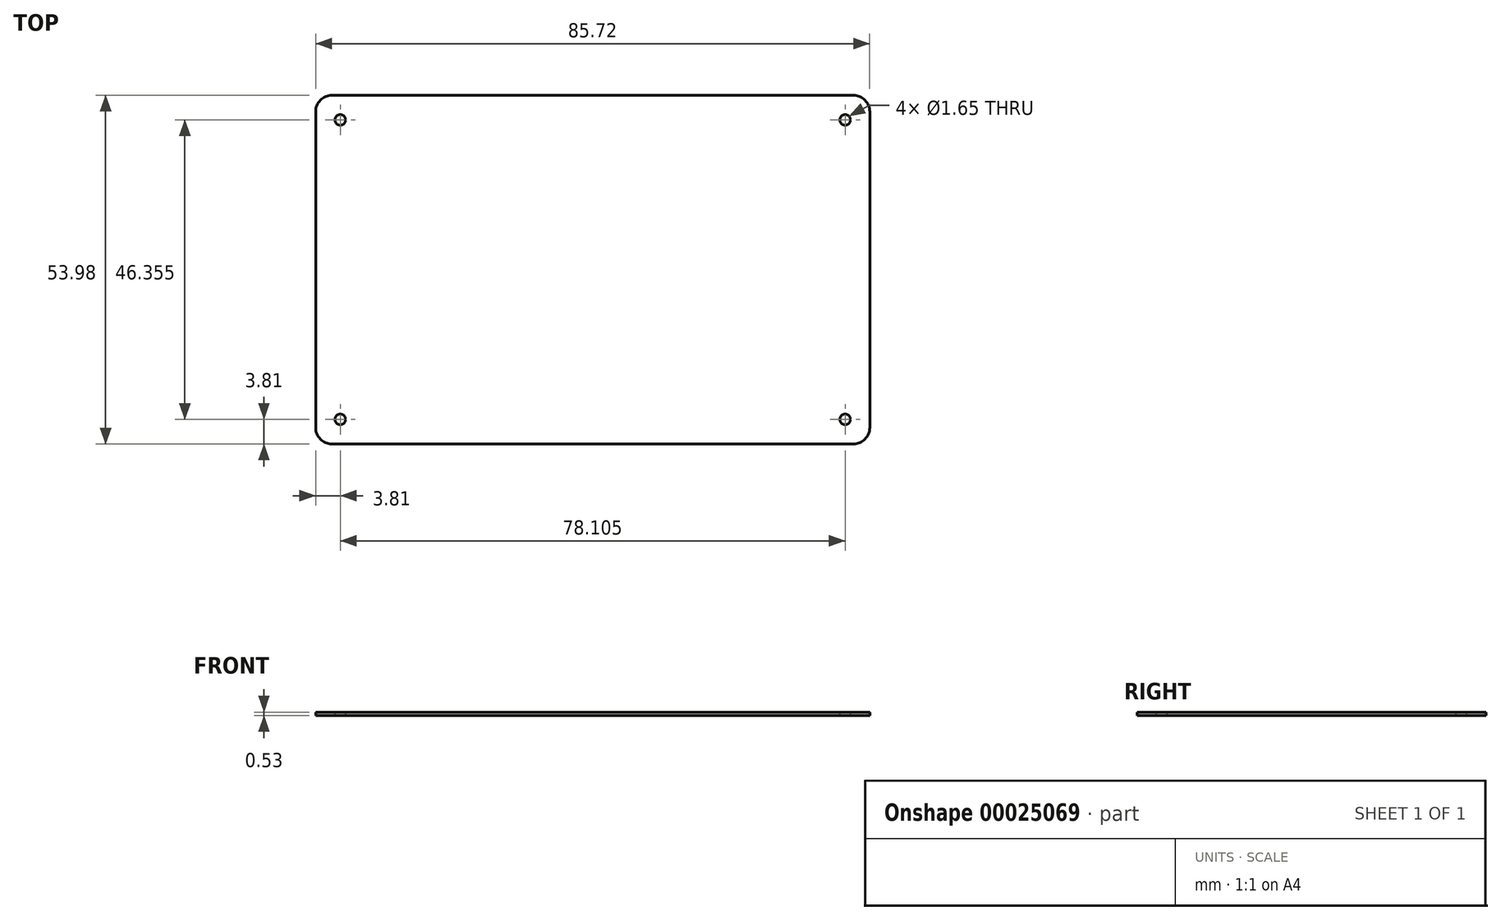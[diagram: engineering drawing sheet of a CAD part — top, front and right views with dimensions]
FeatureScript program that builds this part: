
annotation { "Feature Type Name" : "Feature", "Feature Type Description" : "" }
export const myFeature = defineFeature(function(context is Context, id is Id, definition is map)
    precondition{}
    {
        {
            var Q0;
            Q0=qCreatedBy(makeId("Top.planeOp"),FACE);
            var sketch = newSketch(context, id + "F0", { "sketchPlane" : qUnion([Q0])});
            skLineSegment(sketch, "E0.bottom", {"start": v(2.54, 0) * mm, "end": v(83.19, 0) * mm});
            skLineSegment(sketch, "E0.top", {"start": v(2.54, 53.98) * mm, "end": v(83.19, 53.98) * mm});
            skLineSegment(sketch, "E0.left", {"start": v(0, 2.54) * mm, "end": v(0, 51.44) * mm});
            skLineSegment(sketch, "E0.right", {"start": v(85.73, 2.54) * mm, "end": v(85.73, 51.44) * mm});
            skPoint(sketch, "E1.visualSharp", {"position": v(85.73, 53.98) * mm});
            skArc(sketch, "E1.filletArc", {"start": v(85.73, 51.44) * mm, "mid": v(84.98, 53.23) * mm, "end": v(83.19, 53.98) * mm});
            skPoint(sketch, "E2.visualSharp", {"position": v(0, 53.98) * mm});
            skArc(sketch, "E2.filletArc", {"start": v(2.54, 53.98) * mm, "mid": v(0.74, 53.23) * mm, "end": v(0, 51.44) * mm});
            skPoint(sketch, "E3.visualSharp", {"position": v(0, 0) * mm});
            skArc(sketch, "E3.filletArc", {"start": v(0, 2.54) * mm, "mid": v(0.74, 0.74) * mm, "end": v(2.54, 0) * mm});
            skPoint(sketch, "E4.visualSharp", {"position": v(85.73, 0) * mm});
            skArc(sketch, "E4.filletArc", {"start": v(83.19, 0) * mm, "mid": v(84.98, 0.74) * mm, "end": v(85.73, 2.54) * mm});
            skSolve(sketch);
        }
        {
            var Q0;
            Q0=makeQuery(id+"F0.imprint","IMPRINT",FACE,{"disambiguationData":[TD([[makeQuery(id+"F0.imprint","IMPRINT",EDGE,{"derivedFrom":sQuery(id+"F0.wireOp",EDGE,"E0.bottom")}),1.0]])]});
            extrude(context, id + "F1", {"entities" : qUnion([Q0]), "oppositeDirection" : true, "depth" : 0.53 * mm});
        }
        {
            var Q0;
            Q0=makeQuery(id+"F1.opExtrude","CAP_FACE",FACE,{"disambiguationData":[OSD([sQuery(id+"F0.wireOp",EDGE,"E0.bottom"),sQuery(id+"F0.wireOp",EDGE,"E0.top"),sQuery(id+"F0.wireOp",EDGE,"E0.left"),sQuery(id+"F0.wireOp",EDGE,"E0.right"),sQuery(id+"F0.wireOp",EDGE,"E1.filletArc"),sQuery(id+"F0.wireOp",EDGE,"E2.filletArc"),sQuery(id+"F0.wireOp",EDGE,"E3.filletArc"),sQuery(id+"F0.wireOp",EDGE,"E4.filletArc")])],"isStart":true});
            var sketch = newSketch(context, id + "F2", { "sketchPlane" : qUnion([Q0])});
            skLineSegment(sketch, "E5.0", {"start": v(2.54, 55.25) * mm, "end": v(83.19, 55.25) * mm});
            skArc(sketch, "E5.1", {"start": v(87, 51.44) * mm, "mid": v(85.88, 54.13) * mm, "end": v(83.19, 55.25) * mm});
            skLineSegment(sketch, "E5.2", {"start": v(87, 2.54) * mm, "end": v(87, 51.44) * mm});
            skArc(sketch, "E6.0", {"start": v(2.54, 55.25) * mm, "mid": v(-0.15, 54.13) * mm, "end": v(-1.27, 51.44) * mm});
            skLineSegment(sketch, "E6.1", {"start": v(-1.27, 2.54) * mm, "end": v(-1.27, 51.44) * mm});
            skArc(sketch, "E6.2", {"start": v(-1.27, 2.54) * mm, "mid": v(-0.15, -0.15) * mm, "end": v(2.54, -1.27) * mm});
            skLineSegment(sketch, "E6.3", {"start": v(2.54, -1.27) * mm, "end": v(83.19, -1.27) * mm});
            skArc(sketch, "E6.4", {"start": v(83.19, -1.27) * mm, "mid": v(85.88, -0.15) * mm, "end": v(87, 2.54) * mm});
            skLineSegment(sketch, "E7.bottom", {"start": v(81.92, 50.16) * mm, "end": v(3.8, 50.16) * mm, "construction": true});
            skLineSegment(sketch, "E7.top", {"start": v(81.92, 3.81) * mm, "end": v(3.81, 3.8) * mm, "construction": true});
            skLineSegment(sketch, "E7.left", {"start": v(81.92, 50.16) * mm, "end": v(81.92, 3.81) * mm, "construction": true});
            skLineSegment(sketch, "E7.right", {"start": v(3.8, 50.16) * mm, "end": v(3.81, 3.8) * mm, "construction": true});
            skCircle(sketch, "E8", {"center": v(81.92, 50.16) * mm, "radius": 0.83 * mm});
            skCircle(sketch, "E9", {"center": v(81.92, 3.81) * mm, "radius": 0.83 * mm});
            skCircle(sketch, "E10", {"center": v(3.81, 3.8) * mm, "radius": 0.83 * mm});
            skCircle(sketch, "E11", {"center": v(3.8, 50.16) * mm, "radius": 0.83 * mm});
            skSolve(sketch);
        }
        {
            var Q0;
            Q0=makeQuery(id+"F2.imprint","IMPRINT",FACE,{"disambiguationData":[TD([[makeQuery(id+"F2.imprint","IMPRINT",EDGE,{"derivedFrom":sQuery(id+"F2.wireOp",EDGE,"E9")}),1.0]])]});
            var Q1;
            Q1=makeQuery(id+"F2.imprint","IMPRINT",FACE,{"disambiguationData":[TD([[makeQuery(id+"F2.imprint","IMPRINT",EDGE,{"derivedFrom":sQuery(id+"F2.wireOp",EDGE,"E11")}),1.0]])]});
            var Q2;
            Q2=makeQuery(id+"F2.imprint","IMPRINT",FACE,{"disambiguationData":[TD([[makeQuery(id+"F2.imprint","IMPRINT",EDGE,{"derivedFrom":sQuery(id+"F2.wireOp",EDGE,"E10")}),1.0]])]});
            var Q3;
            Q3=makeQuery(id+"F2.imprint","IMPRINT",FACE,{"disambiguationData":[TD([[makeQuery(id+"F2.imprint","IMPRINT",EDGE,{"derivedFrom":sQuery(id+"F2.wireOp",EDGE,"E8")}),1.0]])]});
            extrude(context, id + "F3", {"entities" : qUnion([Q0, Q1, Q2, Q3]), "operationType" : NewBodyOperationType.REMOVE, "oppositeDirection" : true, "depth" : 25.4 * mm});
        }
    });
